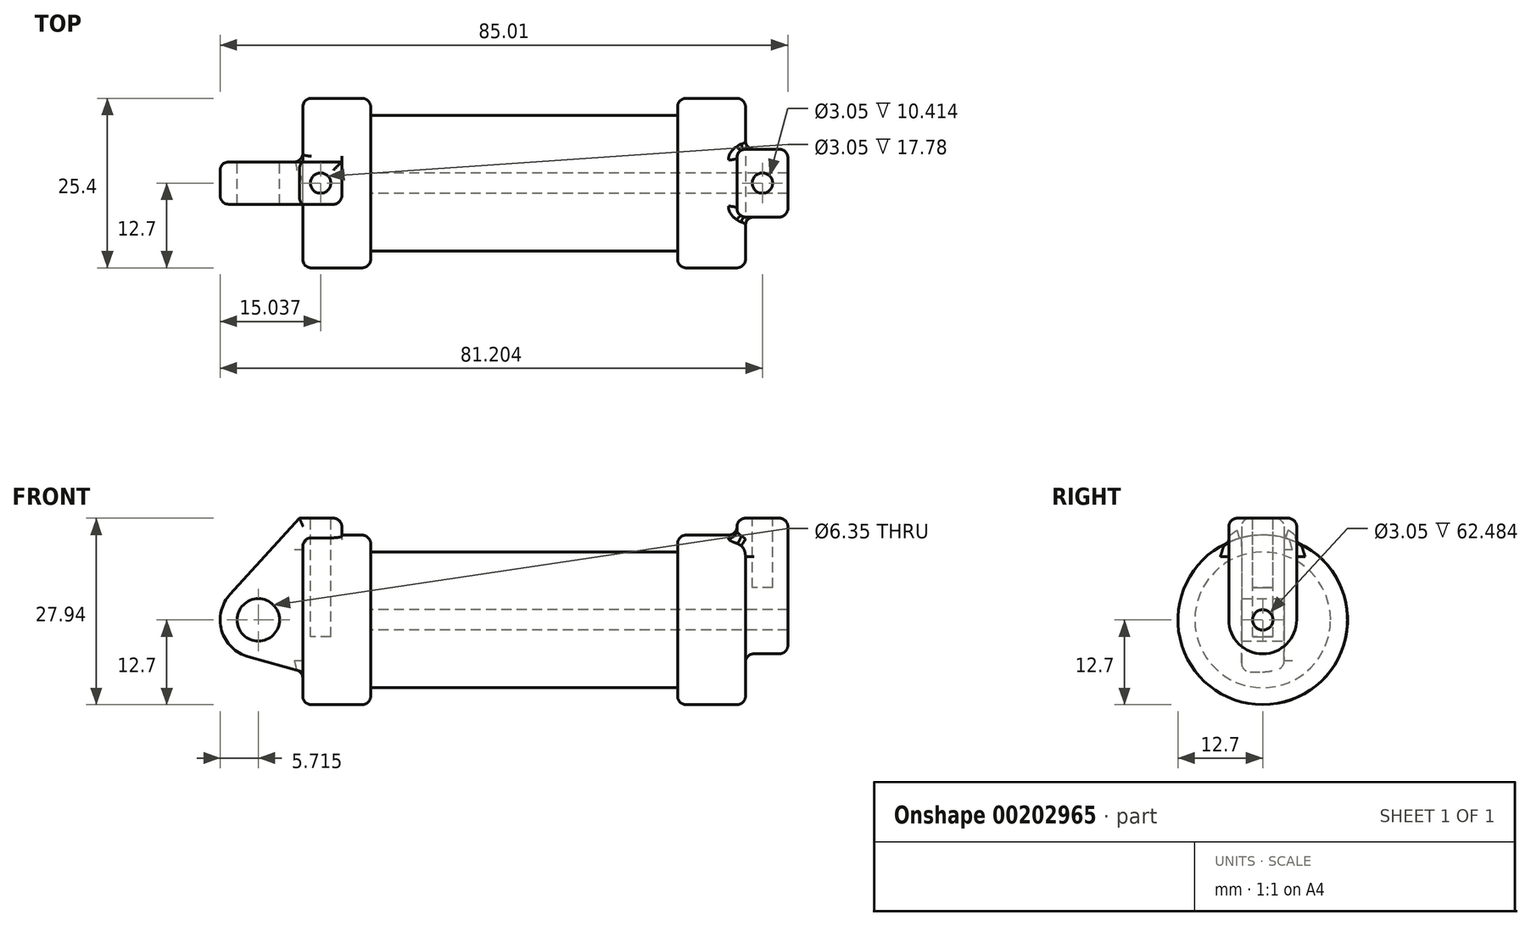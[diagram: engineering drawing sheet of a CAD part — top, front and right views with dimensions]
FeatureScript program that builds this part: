
annotation { "Feature Type Name" : "Feature", "Feature Type Description" : "" }
export const myFeature = defineFeature(function(context is Context, id is Id, definition is map)
    precondition{}
    {
        {
            var Q0;
            Q0=qCreatedBy(makeId("Front.planeOp"),FACE);
            var sketch = newSketch(context, id + "F0", { "sketchPlane" : qUnion([Q0])});
            skLineSegment(sketch, "E0", {"start": v(0, 0) * mm, "end": v(0, 12.7) * mm});
            skLineSegment(sketch, "E1", {"start": v(0, 12.7) * mm, "end": v(10.16, 12.7) * mm});
            skLineSegment(sketch, "E2", {"start": v(10.16, 12.7) * mm, "end": v(10.16, 10.16) * mm});
            skLineSegment(sketch, "E3", {"start": v(10.16, 10.16) * mm, "end": v(56.13, 10.16) * mm});
            skLineSegment(sketch, "E4", {"start": v(56.13, 10.16) * mm, "end": v(56.13, 12.7) * mm});
            skLineSegment(sketch, "E5", {"start": v(56.13, 12.7) * mm, "end": v(66.3, 12.7) * mm});
            skLineSegment(sketch, "E6", {"start": v(66.3, 12.7) * mm, "end": v(66.3, 0) * mm});
            skLineSegment(sketch, "E7", {"start": v(66.3, 0) * mm, "end": v(0, 0) * mm});
            skLineSegment(sketch, "E8", {"start": v(5.84, 15.24) * mm, "end": v(-0.5, 15.24) * mm});
            skLineSegment(sketch, "E9", {"start": v(-0.5, 15.24) * mm, "end": v(-10.88, 3.85) * mm});
            skLineSegment(sketch, "E10", {"start": v(0, 0) * mm, "end": v(-6.65, 0) * mm});
            skCircle(sketch, "E11", {"center": v(-6.65, 0) * mm, "radius": 5.72 * mm});
            skCircle(sketch, "E12", {"center": v(-6.65, 0) * mm, "radius": 3.18 * mm});
            skLineSegment(sketch, "E13", {"start": v(5.84, 15.24) * mm, "end": v(5.84, -9.4) * mm});
            skLineSegment(sketch, "E14", {"start": v(5.84, -9.4) * mm, "end": v(-8.18, -5.5) * mm});
            skLineSegment(sketch, "E15", {"start": v(0, 0) * mm, "end": v(0, -7.78) * mm});
            skSolve(sketch);
        }
        {
            var Q0;
            {var subQ0=sQuery(id+"F0.wireOp",EDGE,"E0");Q0=makeQuery(id+"F0.imprint","IMPRINT",FACE,{"disambiguationData":[TD([[makeQuery(id+"F0.imprint","IMPRINT",EDGE,{"derivedFrom":subQ0}),-1.0]])]});}
            var Q1;
            {var subQ0=sQuery(id+"F0.wireOp",EDGE,"E2");Q1=makeQuery(id+"F0.imprint","IMPRINT",FACE,{"disambiguationData":[TD([[makeQuery(id+"F0.imprint","IMPRINT",EDGE,{"derivedFrom":subQ0}),-1.0]])]});}
            var Q2;
            Q2=sQuery(id+"F0.wireOp",EDGE,"E7");
            revolve(context, id + "F1", {"entities" : qUnion([Q0, Q1]), "axis" : qUnion([Q2]), "revolveType" : RevolveType.FULL});
        }
        {
            var Q0;
            {var subQ3=sQuery(id+"F0.wireOp",EDGE,"E0");Q0=makeQuery(id+"F0.imprint","IMPRINT",FACE,{"disambiguationData":[TD([[makeQuery(id+"F0.imprint","IMPRINT",EDGE,{"derivedFrom":subQ3}),1.0]])]});}
            var Q1;
            {var subQ4=sQuery(id+"F0.wireOp",EDGE,"E12");Q1=makeQuery(id+"F0.imprint","IMPRINT",FACE,{"disambiguationData":[TD([[makeQuery(id+"F0.imprint","IMPRINT",EDGE,{"derivedFrom":subQ4}),-1.0]])]});}
            var Q2;
            {var subQ0=sQuery(id+"F0.wireOp",EDGE,"E15");Q2=makeQuery(id+"F0.imprint","IMPRINT",FACE,{"disambiguationData":[TD([[makeQuery(id+"F0.imprint","IMPRINT",EDGE,{"derivedFrom":subQ0}),-1.0]])]});}
            var Q3;
            {var subQ0=sQuery(id+"F0.wireOp",EDGE,"E0");Q3=makeQuery(id+"F0.imprint","IMPRINT",FACE,{"disambiguationData":[TD([[makeQuery(id+"F0.imprint","IMPRINT",EDGE,{"derivedFrom":subQ0}),-1.0]])]});}
            var Q4;
            {var subQ0=sQuery(id+"F0.wireOp",EDGE,"E15");Q4=makeQuery(id+"F0.imprint","IMPRINT",FACE,{"disambiguationData":[TD([[makeQuery(id+"F0.imprint","IMPRINT",EDGE,{"derivedFrom":subQ0}),1.0]])]});}
            extrude(context, id + "F2", {"entities" : qUnion([Q0, Q1, Q2, Q3, Q4]), "operationType" : NewBodyOperationType.ADD, "endBound" : BoundingType.SYMMETRIC, "depth" : 6.35 * mm});
        }
        {
            var Q0;
            Q0=makeQuery(id+"F1.opRevolve","SWEPT_FACE",FACE,{"disambiguationData":[OSD([sQuery(id+"F0.wireOp",EDGE,"E6")])]});
            var sketch = newSketch(context, id + "F3", { "sketchPlane" : qUnion([Q0])});
            skCircle(sketch, "E16", {"center": v(0, 0) * mm, "radius": 1.52 * mm});
            skCircle(sketch, "E17", {"center": v(0, 0) * mm, "radius": 5.08 * mm});
            skLineSegment(sketch, "E18", {"start": v(5.08, 0) * mm, "end": v(5.08, 15.24) * mm});
            skLineSegment(sketch, "E19", {"start": v(-5.08, 0) * mm, "end": v(-5.08, 15.24) * mm});
            skLineSegment(sketch, "E20", {"start": v(-5.08, 15.24) * mm, "end": v(5.08, 15.24) * mm});
            skSolve(sketch);
        }
        {
            var Q0;
            {var subQ0=sQuery(id+"F3.wireOp",EDGE,"E20");Q0=makeQuery(id+"F3.imprint","IMPRINT",FACE,{"disambiguationData":[TD([[makeQuery(id+"F3.imprint","IMPRINT",EDGE,{"derivedFrom":subQ0}),-1.0]])]});}
            var Q1;
            {var subQ0=sQuery(id+"F3.wireOp",EDGE,"E18");var subQ1=sQuery(id+"F3.wireOp",EDGE,"E17");var subQ2=makeQuery(id+"F3.imprint","INTERSECT",VERTEX,{"derivedFrom":[subQ1,subQ0]});Q1=makeQuery(id+"F3.imprint","IMPRINT",FACE,{"disambiguationData":[TD([[makeQuery(id+"F3.imprint","IMPRINT",EDGE,{"disambiguationData":[TD([[subQ2,-1.0]])],"derivedFrom":subQ1}),-1.0]])]});}
            var Q2;
            Q2=makeQuery(id+"F3.imprint","IMPRINT",FACE,{"disambiguationData":[TD([[makeQuery(id+"F3.imprint","IMPRINT",EDGE,{"derivedFrom":sQuery(id+"F3.wireOp",EDGE,"E16")}),-1.0]])]});
            extrude(context, id + "F4", {"entities" : qUnion([Q0, Q1, Q2]), "operationType" : NewBodyOperationType.ADD, "oppositeDirection" : true, "depth" : 1.27 * mm});
        }
        {
            var Q0;
            {var subQ0=sQuery(id+"F3.wireOp",EDGE,"E20");Q0=makeQuery(id+"F3.imprint","IMPRINT",FACE,{"disambiguationData":[TD([[makeQuery(id+"F3.imprint","IMPRINT",EDGE,{"derivedFrom":subQ0}),-1.0]])]});}
            var Q1;
            {var subQ0=sQuery(id+"F3.wireOp",EDGE,"E18");var subQ1=sQuery(id+"F3.wireOp",EDGE,"E17");var subQ2=makeQuery(id+"F3.imprint","INTERSECT",VERTEX,{"derivedFrom":[subQ1,subQ0]});Q1=makeQuery(id+"F3.imprint","IMPRINT",FACE,{"disambiguationData":[TD([[makeQuery(id+"F3.imprint","IMPRINT",EDGE,{"disambiguationData":[TD([[subQ2,-1.0]])],"derivedFrom":subQ1}),-1.0]])]});}
            var Q2;
            Q2=makeQuery(id+"F3.imprint","IMPRINT",FACE,{"disambiguationData":[TD([[makeQuery(id+"F3.imprint","IMPRINT",EDGE,{"derivedFrom":sQuery(id+"F3.wireOp",EDGE,"E16")}),-1.0]])]});
            extrude(context, id + "F5", {"entities" : qUnion([Q0, Q1, Q2]), "operationType" : NewBodyOperationType.ADD, "depth" : 6.35 * mm});
        }
        {
            var Q0;
            Q0=makeQuery(id+"F3.imprint","IMPRINT",FACE,{"disambiguationData":[TD([[makeQuery(id+"F3.imprint","IMPRINT",EDGE,{"derivedFrom":sQuery(id+"F3.wireOp",EDGE,"E16")}),1.0]])]});
            var Q1;
            Q1=makeQuery(id+"F1.opRevolve","SWEPT_FACE",FACE,{"disambiguationData":[OSD([sQuery(id+"F0.wireOp",EDGE,"E2")])]});
            extrude(context, id + "F6", {"entities" : qUnion([Q0]), "operationType" : NewBodyOperationType.REMOVE, "endBound" : BoundingType.UP_TO_SURFACE, "oppositeDirection" : true, "endBoundEntityFace" : qUnion([Q1]), "depth" : 25.4 * mm});
        }
        {
            var Q0;
            {var subQ0=sQuery(id+"F3.wireOp",EDGE,"E20");Q0=makeQuery(id+"F5.boolean.opBoolean","MERGE",FACE,{"derivedFrom":[makeQuery(id+"F4.opExtrude","SWEPT_FACE",FACE,{"disambiguationData":[OSD([subQ0])]}),makeQuery(id+"F5.opExtrude","SWEPT_FACE",FACE,{"disambiguationData":[OSD([subQ0])]})]});}
            var sketch = newSketch(context, id + "F7", { "sketchPlane" : qUnion([Q0])});
            skCircle(sketch, "E21", {"center": v(68.83, 0) * mm, "radius": 1.52 * mm});
            skPoint(sketch, "E21.centerSnap0", {"position": v(68.83, 5.08) * mm});
            skPoint(sketch, "E21.centerSnap1", {"position": v(65.02, 0) * mm});
            skCircle(sketch, "E22", {"center": v(2.67, 0) * mm, "radius": 1.52 * mm});
            skSolve(sketch);
        }
        {
            var Q0;
            Q0=makeQuery(id+"F7.imprint","IMPRINT",FACE,{"disambiguationData":[TD([[makeQuery(id+"F7.imprint","IMPRINT",EDGE,{"derivedFrom":sQuery(id+"F7.wireOp",EDGE,"E21")}),1.0]])]});
            extrude(context, id + "F8", {"entities" : qUnion([Q0]), "operationType" : NewBodyOperationType.REMOVE, "oppositeDirection" : true, "depth" : 10.4 * mm});
        }
        {
            var Q0;
            Q0=makeQuery(id+"F7.imprint","IMPRINT",FACE,{"disambiguationData":[TD([[makeQuery(id+"F7.imprint","IMPRINT",EDGE,{"derivedFrom":sQuery(id+"F7.wireOp",EDGE,"E22")}),1.0]])]});
            extrude(context, id + "F9", {"entities" : qUnion([Q0]), "operationType" : NewBodyOperationType.REMOVE, "oppositeDirection" : true, "depth" : 17.78 * mm});
        }
        {
            var Q0;
            Q0=makeQuery(id+"F1.opRevolve","SWEPT_EDGE",EDGE,{"disambiguationData":[OSD([sQuery(id+"F0.wireOp",EDGE,"E5"),sQuery(id+"F0.wireOp",EDGE,"E6")])]});
            var Q1;
            Q1=makeQuery(id+"F1.opRevolve","SWEPT_EDGE",EDGE,{"disambiguationData":[OSD([sQuery(id+"F0.wireOp",EDGE,"E4"),sQuery(id+"F0.wireOp",EDGE,"E5")])]});
            var Q2;
            Q2=makeQuery(id+"F1.opRevolve","SWEPT_EDGE",EDGE,{"disambiguationData":[OSD([sQuery(id+"F0.wireOp",EDGE,"E1"),sQuery(id+"F0.wireOp",EDGE,"E2")])]});
            var Q3;
            Q3=makeQuery(id+"F1.opRevolve","SWEPT_EDGE",EDGE,{"disambiguationData":[OSD([sQuery(id+"F0.wireOp",EDGE,"E0"),sQuery(id+"F0.wireOp",EDGE,"E1")])]});
            fillet(context, id + "F10", {"entities" : qUnion([Q0, Q1, Q2, Q3]), "radius" : 1.27 * mm, "tangentPropagation" : true, "allowEdgeOverflow" : false});
        }
        {
            var Q0;
            Q0=makeQuery(id+"F2.opExtrude","CAP_EDGE",EDGE,{"disambiguationData":[OSD([sQuery(id+"F0.wireOp",EDGE,"E14")])],"isStart":false});
            var Q1;
            Q1=makeQuery(id+"F2.opExtrude","CAP_EDGE",EDGE,{"disambiguationData":[OSD([sQuery(id+"F0.wireOp",EDGE,"E14")])],"isStart":true});
            var Q2;
            Q2=makeQuery(id+"F2.boolean.opBoolean","INTERSECT",EDGE,{"derivedFrom":[makeQuery(id+"F1.opRevolve","SWEPT_FACE",FACE,{"disambiguationData":[OSD([sQuery(id+"F0.wireOp",EDGE,"E0")])]}),makeQuery(id+"F2.opExtrude","CAP_FACE",FACE,{"disambiguationData":[OSD([sQuery(id+"F0.wireOp",EDGE,"E8"),sQuery(id+"F0.wireOp",EDGE,"E9"),sQuery(id+"F0.wireOp",EDGE,"E11"),sQuery(id+"F0.wireOp",EDGE,"E12"),sQuery(id+"F0.wireOp",EDGE,"E13"),sQuery(id+"F0.wireOp",EDGE,"E14")])],"isStart":true})]});
            var Q3;
            Q3=makeQuery(id+"F2.opExtrude","SWEPT_EDGE",EDGE,{"disambiguationData":[OSD([sQuery(id+"F0.wireOp",EDGE,"E8"),sQuery(id+"F0.wireOp",EDGE,"E13")])]});
            var Q4;
            Q4=makeQuery(id+"F2.opExtrude","CAP_EDGE",EDGE,{"disambiguationData":[OSD([sQuery(id+"F0.wireOp",EDGE,"E8")])],"isStart":false});
            var Q5;
            Q5=makeQuery(id+"F2.opExtrude","CAP_EDGE",EDGE,{"disambiguationData":[OSD([sQuery(id+"F0.wireOp",EDGE,"E8")])],"isStart":true});
            var Q6;
            Q6=makeQuery(id+"F2.opExtrude","CAP_EDGE",EDGE,{"disambiguationData":[OSD([sQuery(id+"F0.wireOp",EDGE,"E13")])],"isStart":false});
            fillet(context, id + "F11", {"entities" : qUnion([Q0, Q1, Q2, Q3, Q4, Q5, Q6]), "radius" : 1.27 * mm, "tangentPropagation" : true, "allowEdgeOverflow" : false});
        }
        {
            var Q0;
            Q0=makeQuery(id+"F5.opExtrude","CAP_EDGE",EDGE,{"disambiguationData":[OSD([sQuery(id+"F3.wireOp",EDGE,"E18")])],"isStart":false});
            var Q1;
            Q1=makeQuery(id+"F5.opExtrude","CAP_EDGE",EDGE,{"disambiguationData":[OSD([sQuery(id+"F3.wireOp",EDGE,"E20")])],"isStart":false});
            var Q2;
            {var subQ0=sQuery(id+"F3.wireOp",EDGE,"E20");var subQ1=sQuery(id+"F3.wireOp",EDGE,"E19");Q2=makeQuery(id+"F5.boolean.opBoolean","MERGE",EDGE,{"derivedFrom":[makeQuery(id+"F4.opExtrude","SWEPT_EDGE",EDGE,{"disambiguationData":[OSD([subQ1,subQ0])]}),makeQuery(id+"F5.opExtrude","SWEPT_EDGE",EDGE,{"disambiguationData":[OSD([subQ1,subQ0])]})]});}
            var Q3;
            {var subQ0=sQuery(id+"F3.wireOp",EDGE,"E20");var subQ1=sQuery(id+"F3.wireOp",EDGE,"E18");Q3=makeQuery(id+"F5.boolean.opBoolean","MERGE",EDGE,{"derivedFrom":[makeQuery(id+"F4.opExtrude","SWEPT_EDGE",EDGE,{"disambiguationData":[OSD([subQ1,subQ0])]}),makeQuery(id+"F5.opExtrude","SWEPT_EDGE",EDGE,{"disambiguationData":[OSD([subQ1,subQ0])]})]});}
            var Q4;
            Q4=makeQuery(id+"F4.opExtrude","CAP_EDGE",EDGE,{"disambiguationData":[OSD([sQuery(id+"F3.wireOp",EDGE,"E20")])],"isStart":false});
            var Q5;
            Q5=makeQuery(id+"F5.opExtrude","CAP_EDGE",EDGE,{"disambiguationData":[OSD([sQuery(id+"F3.wireOp",EDGE,"E18")])],"isStart":true});
            var Q6;
            Q6=makeQuery(id+"F4.boolean.opBoolean","INTERSECT",EDGE,{"derivedFrom":[makeQuery(id+"F1.opRevolve","SWEPT_FACE",FACE,{"disambiguationData":[OSD([sQuery(id+"F0.wireOp",EDGE,"E5")])]}),makeQuery(id+"F4.opExtrude","CAP_FACE",FACE,{"disambiguationData":[OSD([sQuery(id+"F3.wireOp",EDGE,"E16"),sQuery(id+"F3.wireOp",EDGE,"E17"),sQuery(id+"F3.wireOp",EDGE,"E18"),sQuery(id+"F3.wireOp",EDGE,"E19"),sQuery(id+"F3.wireOp",EDGE,"E20")])],"isStart":false})]});
            var Q7;
            Q7=makeQuery(id+"F4.opExtrude","CAP_EDGE",EDGE,{"disambiguationData":[OSD([sQuery(id+"F3.wireOp",EDGE,"E19")])],"isStart":false});
            var Q8;
            Q8=makeQuery(id+"F4.opExtrude","CAP_EDGE",EDGE,{"disambiguationData":[OSD([sQuery(id+"F3.wireOp",EDGE,"E18")])],"isStart":false});
            fillet(context, id + "F12", {"entities" : qUnion([Q0, Q1, Q2, Q3, Q4, Q5, Q6, Q7, Q8]), "radius" : 1.27 * mm, "tangentPropagation" : true, "allowEdgeOverflow" : false});
        }
    });
